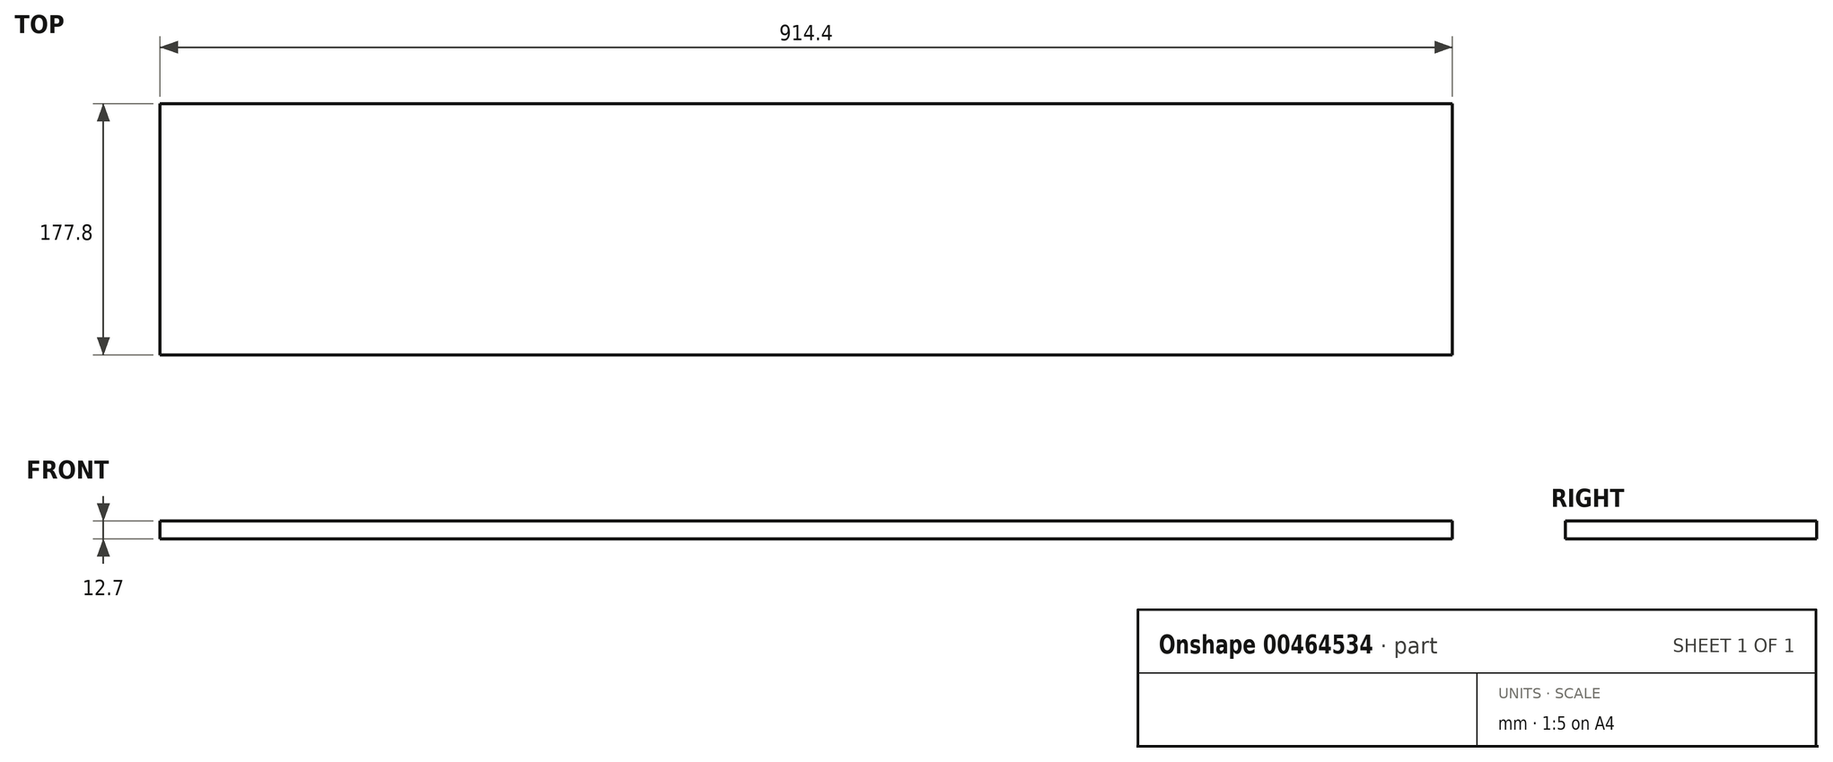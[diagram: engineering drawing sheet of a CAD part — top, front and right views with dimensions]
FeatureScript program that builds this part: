
annotation { "Feature Type Name" : "Feature", "Feature Type Description" : "" }
export const myFeature = defineFeature(function(context is Context, id is Id, definition is map)
    precondition{}
    {
        {
            var Q0;
            Q0=qCreatedBy(makeId("Top.planeOp"),FACE);
            var sketch = newSketch(context, id + "F0", { "sketchPlane" : qUnion([Q0])});
            skLineSegment(sketch, "E0.bottom", {"start": v(457.2, -88.9) * mm, "end": v(-457.2, -88.9) * mm});
            skLineSegment(sketch, "E0.top", {"start": v(457.2, 88.9) * mm, "end": v(-457.2, 88.9) * mm});
            skLineSegment(sketch, "E0.left", {"start": v(457.2, -88.9) * mm, "end": v(457.2, 88.9) * mm});
            skLineSegment(sketch, "E0.right", {"start": v(-457.2, -88.9) * mm, "end": v(-457.2, 88.9) * mm});
            skPoint(sketch, "E0.middle", {"position": v(0, 0) * mm});
            skSolve(sketch);
        }
        {
            var Q0;
            Q0 = qSketchRegion(id + "F0", true);
            extrude(context, id + "F1", {"entities" : qUnion([Q0]), "depth" : 12.7 * mm});
        }
    });
